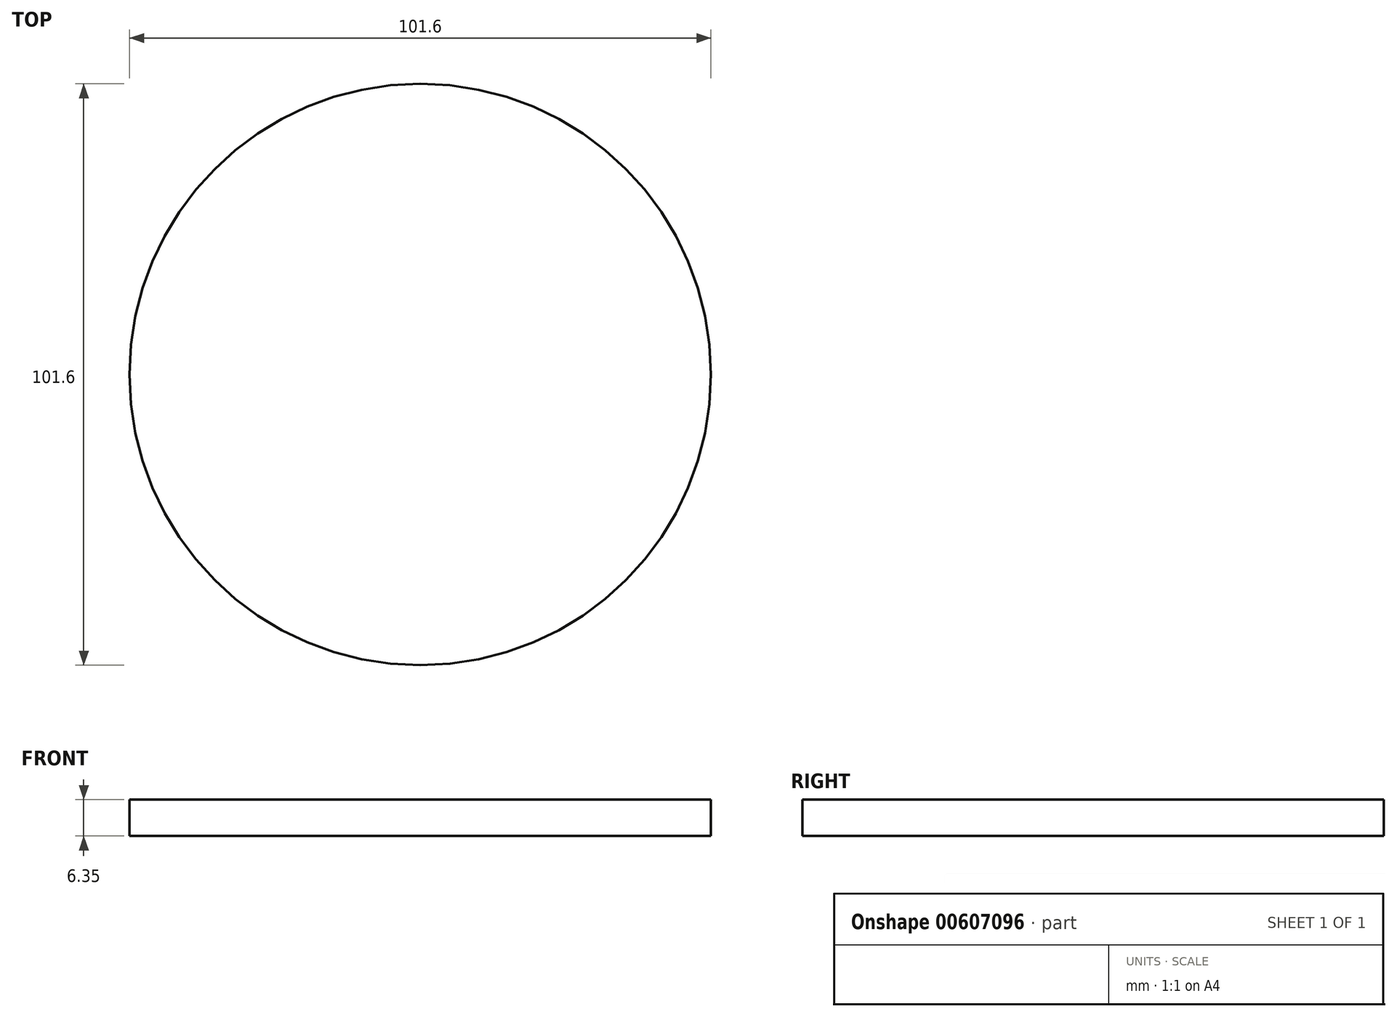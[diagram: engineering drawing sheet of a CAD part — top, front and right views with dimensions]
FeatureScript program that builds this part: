
annotation { "Feature Type Name" : "Feature", "Feature Type Description" : "" }
export const myFeature = defineFeature(function(context is Context, id is Id, definition is map)
    precondition{}
    {
        {
            var Q0;
            Q0=qCreatedBy(makeId("Top.planeOp"),FACE);
            var sketch = newSketch(context, id + "F0", { "sketchPlane" : qUnion([Q0])});
            skCircle(sketch, "E0", {"center": v(0, 0) * mm, "radius": 50.8 * mm});
            skSolve(sketch);
        }
        {
            var Q0;
            Q0=makeQuery(id+"F0.imprint","IMPRINT",FACE,{"disambiguationData":[TD([[makeQuery(id+"F0.imprint","IMPRINT",EDGE,{"derivedFrom":sQuery(id+"F0.wireOp",EDGE,"E0")}),1.0]])]});
            extrude(context, id + "F1", {"entities" : qUnion([Q0]), "depth" : 6.35 * mm, "offsetDistance" : 25.4 * mm});
        }
    });
